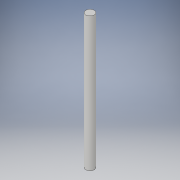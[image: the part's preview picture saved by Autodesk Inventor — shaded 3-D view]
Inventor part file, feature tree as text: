
AUTODESK INVENTOR PART (.ipt)
format: ipt  version: 2019 (Build 230136000, 136)  size: 96,256 bytes
history: native  units: in
note: dims shown in document units (in); Inventor stores cm internally (conversion verified against a paired STEP export)
features: extrude x1
ambient origin geometry x8: Origin, YZ Plane, XZ Plane, XY Plane, X Axis, Y Axis, Z Axis, Center Point
bodies: Solid3 (feature_tree)
feature tree (1):
  extrude  "Extrude2"  [1 undecoded]
note: 1 required parameter value undecoded (feature->parameter linkage not recoverable at this tier; creation-order binding heuristic only, values carry confidence <= 0.55)
